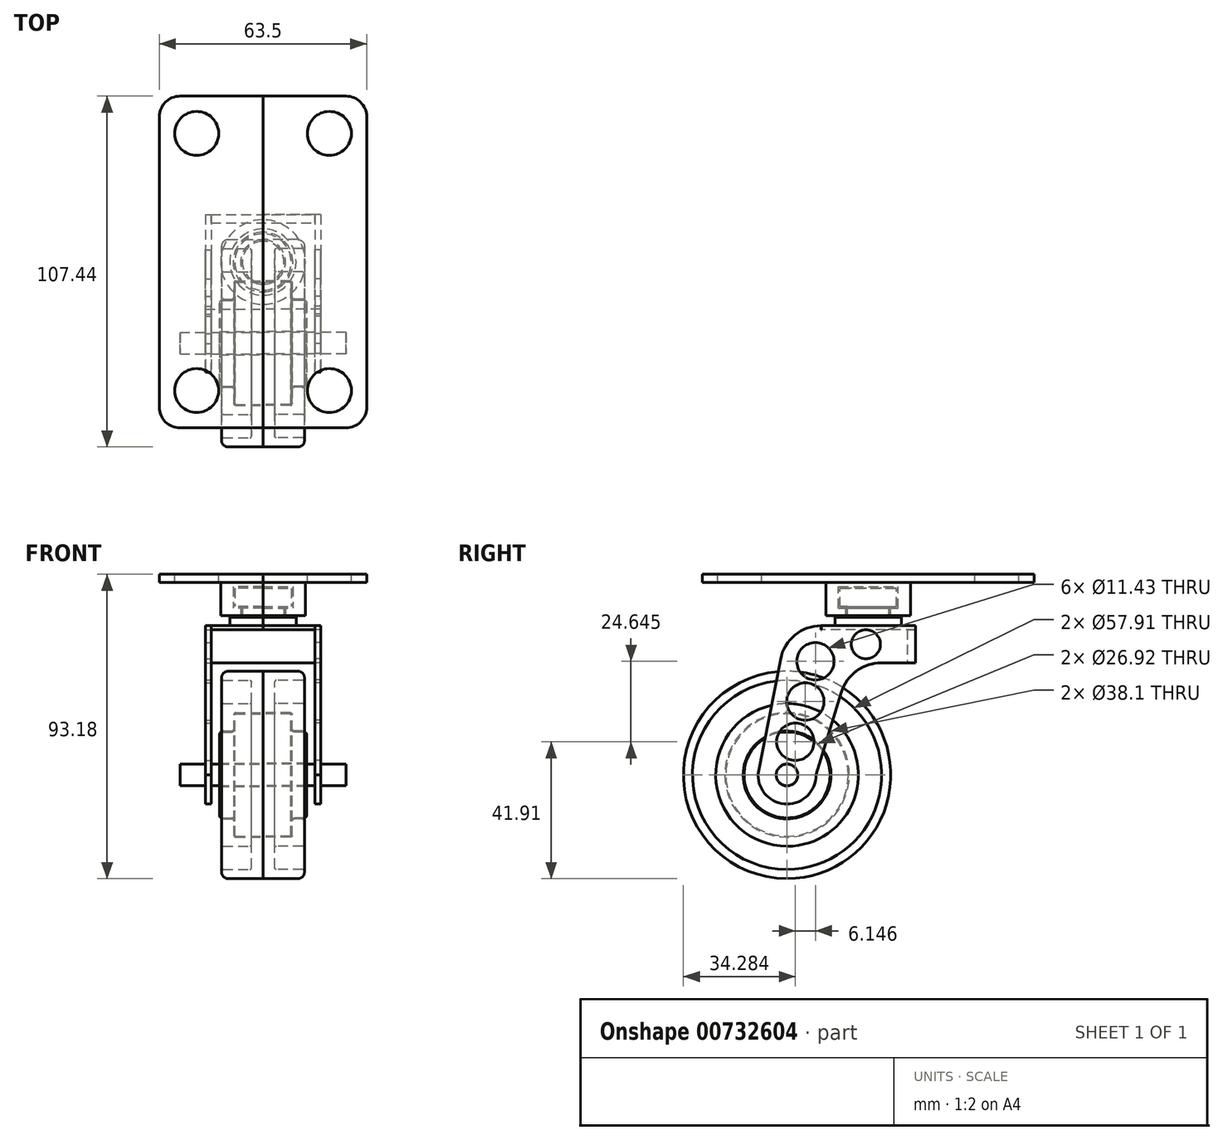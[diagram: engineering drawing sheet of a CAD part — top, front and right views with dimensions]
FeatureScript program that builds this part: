
annotation { "Feature Type Name" : "Feature", "Feature Type Description" : "" }
export const myFeature = defineFeature(function(context is Context, id is Id, definition is map)
    precondition{}
    {
        {
            var Q0;
            Q0=qCreatedBy(makeId("Front.planeOp"),FACE);
            var sketch = newSketch(context, id + "F0", { "sketchPlane" : qUnion([Q0])});
            skLineSegment(sketch, "E0.top", {"start": v(2.03, 31.75) * mm, "end": v(12.7, 31.75) * mm});
            skLineSegment(sketch, "E0.left", {"start": v(0, 29.46) * mm, "end": v(0, 29.72) * mm});
            skLineSegment(sketch, "E1", {"start": v(0, 0) * mm, "end": v(36.08, 0) * mm, "construction": true});
            skLineSegment(sketch, "E2.top", {"start": v(4.32, 19.05) * mm, "end": v(12.7, 19.05) * mm});
            skLineSegment(sketch, "E2.left", {"start": v(3.81, 14.22) * mm, "end": v(3.8, 18.54) * mm});
            skLineSegment(sketch, "E3", {"start": v(0.76, 13.46) * mm, "end": v(3.05, 13.46) * mm});
            skLineSegment(sketch, "E4", {"start": v(12.7, 31.75) * mm, "end": v(12.7, 19.05) * mm});
            skPoint(sketch, "E5.visualSharp", {"position": v(0, 31.75) * mm});
            skArc(sketch, "E5.filletArc", {"start": v(2.03, 31.75) * mm, "mid": v(0.6, 31.15) * mm, "end": v(0, 29.72) * mm});
            skArc(sketch, "E6.filletArc", {"start": v(3.05, 13.46) * mm, "mid": v(3.59, 13.69) * mm, "end": v(3.81, 14.22) * mm});
            skArc(sketch, "E7.filletArc", {"start": v(0, 14.22) * mm, "mid": v(0.22, 13.69) * mm, "end": v(0.76, 13.46) * mm});
            skPoint(sketch, "E8.visualSharp", {"position": v(3.8, 19.05) * mm});
            skArc(sketch, "E8.filletArc", {"start": v(4.32, 19.05) * mm, "mid": v(3.96, 18.9) * mm, "end": v(3.81, 18.54) * mm});
            skLineSegment(sketch, "E9.0", {"start": v(4.32, 18.75) * mm, "end": v(12.7, 18.75) * mm});
            skLineSegment(sketch, "E10.0", {"start": v(3.8, 14.22) * mm, "end": v(3.8, 18.54) * mm});
            skArc(sketch, "E11.0", {"start": v(3.05, 13.16) * mm, "mid": v(3.8, 13.47) * mm, "end": v(4.11, 14.22) * mm});
            skLineSegment(sketch, "E11.1", {"start": v(0.13, 13.16) * mm, "end": v(3.05, 13.16) * mm});
            skArc(sketch, "E11.5", {"start": v(4.32, 18.75) * mm, "mid": v(4.17, 18.69) * mm, "end": v(4.11, 18.54) * mm});
            skLineSegment(sketch, "E12", {"start": v(4.11, 18.54) * mm, "end": v(4.11, 14.22) * mm});
            skLineSegment(sketch, "E13", {"start": v(12.7, 18.75) * mm, "end": v(12.7, 3.56) * mm});
            skPoint(sketch, "E14.visualSharp", {"position": v(0, 13.16) * mm});
            skLineSegment(sketch, "E15.bottom", {"start": v(12.7, 3.56) * mm, "end": v(-0.63, 3.56) * mm});
            skPoint(sketch, "E15.middle", {"position": v(0, 0) * mm});
            skPoint(sketch, "E15.right.end.orphan", {"position": v(-12.7, -3.56) * mm});
            skPoint(sketch, "E15.right.start.orphan", {"position": v(-12.7, 3.56) * mm});
            skPoint(sketch, "E16.orphan", {"position": v(12.7, -3.56) * mm});
            skLineSegment(sketch, "E17.0", {"start": v(-0.63, 3.56) * mm, "end": v(-0.63, 12.4) * mm});
            skPoint(sketch, "E18.visualSharp", {"position": v(-0.63, 13.16) * mm});
            skArc(sketch, "E18.filletArc", {"start": v(0.13, 13.16) * mm, "mid": v(-0.41, 12.93) * mm, "end": v(-0.63, 12.4) * mm});
            skLineSegment(sketch, "E19.bottom", {"start": v(0.5, 28.96) * mm, "end": v(8.64, 28.96) * mm});
            skLineSegment(sketch, "E19.top", {"start": v(0.5, 21.84) * mm, "end": v(8.64, 21.84) * mm});
            skLineSegment(sketch, "E19.left", {"start": v(0, 21.34) * mm, "end": v(0, 14.22) * mm});
            skLineSegment(sketch, "E19.right", {"start": v(9.14, 28.45) * mm, "end": v(9.14, 22.35) * mm});
            skArc(sketch, "E20.filletArc", {"start": v(0, 29.46) * mm, "mid": v(0.15, 29.1) * mm, "end": v(0.5, 28.96) * mm});
            skPoint(sketch, "E21.visualSharp", {"position": v(9.14, 28.96) * mm});
            skArc(sketch, "E21.filletArc", {"start": v(9.14, 28.45) * mm, "mid": v(9, 28.8) * mm, "end": v(8.64, 28.96) * mm});
            skPoint(sketch, "E22.visualSharp", {"position": v(9.14, 21.84) * mm});
            skArc(sketch, "E22.filletArc", {"start": v(8.64, 21.84) * mm, "mid": v(9, 22) * mm, "end": v(9.14, 22.35) * mm});
            skArc(sketch, "E23.filletArc", {"start": v(0.5, 21.84) * mm, "mid": v(0.15, 21.7) * mm, "end": v(0, 21.34) * mm});
            skSolve(sketch);
        }
        {
            var Q0;
            Q0=makeQuery(id+"F0.imprint","IMPRINT",FACE,{"disambiguationData":[TD([[makeQuery(id+"F0.imprint","IMPRINT",EDGE,{"derivedFrom":sQuery(id+"F0.wireOp",EDGE,"E0.top")}),-1.0]])]});
            var Q1;
            Q1=makeQuery(id+"F0.imprint","IMPRINT",FACE,{"disambiguationData":[TD([[makeQuery(id+"F0.imprint","IMPRINT",EDGE,{"derivedFrom":sQuery(id+"F0.wireOp",EDGE,"E9.0")}),-1.0]])]});
            var Q2;
            Q2=sQuery(id+"F0.wireOp",EDGE,"E1");
            revolve(context, id + "F1", {"surfaceOperationType" : NewSurfaceOperationType.NEW, "entities" : qUnion([Q0, Q1]), "axis" : qUnion([Q2]), "revolveType" : RevolveType.ONE_DIRECTION, "oppositeDirection" : true, "angle" : 360 * degree});
        }
        {
            var Q0;
            Q0=makeQuery(id+"F1.opRevolve","SWEPT_FACE",FACE,{"disambiguationData":[OSD([sQuery(id+"F0.wireOp",EDGE,"E17.0")])]});
            cPlane(context, id + "F2", {"entities" : qUnion([Q0]), "cplaneType" : CPlaneType.OFFSET, "offset" : 2.54 * mm, "width" : 152.4 * mm, "height" : 152.4 * mm});
        }
        {
            var Q0;
            Q0=makeQuery(id+"F1.opRevolve","SWEPT_FACE",FACE,{"disambiguationData":[OSD([sQuery(id+"F0.wireOp",EDGE,"E13")])]});
            var sketch = newSketch(context, id + "F3", { "sketchPlane" : qUnion([Q0])});
            skCircle(sketch, "E24", {"center": v(0, 0) * mm, "radius": 3.3 * mm});
            skSolve(sketch);
        }
        {
            var Q0;
            Q0 = qSketchRegion(id + "F3", true);
            extrude(context, id + "F4", {"entities" : qUnion([Q0]), "oppositeDirection" : true, "depth" : 25.4 * mm, "offsetDistance" : 25.4 * mm});
        }
        {
            var Q0;
            Q0=qCreatedBy(id+"F2.planeOp",FACE);
            var sketch = newSketch(context, id + "F5", { "sketchPlane" : qUnion([Q0])});
            skCircle(sketch, "E25", {"center": v(0, 0) * mm, "radius": 3.3 * mm});
            skArc(sketch, "E26", {"start": v(-8.9, 0) * mm, "mid": v(0, -8.9) * mm, "end": v(8.9, 0) * mm});
            skLineSegment(sketch, "E27.bottom", {"start": v(-39.37, 45.72) * mm, "end": v(-10.47, 45.72) * mm});
            skLineSegment(sketch, "E27.top", {"start": v(-39.37, 34.3) * mm, "end": v(-28.77, 34.3) * mm});
            skLineSegment(sketch, "E27.left", {"start": v(-39.37, 45.72) * mm, "end": v(-39.37, 34.3) * mm});
            skLineSegment(sketch, "E28", {"start": v(8.9, 0) * mm, "end": v(2, 35.44) * mm});
            skLineSegment(sketch, "E29", {"start": v(-8.89, 0) * mm, "end": v(-16.63, 25.3) * mm});
            skPoint(sketch, "E30.visualSharp", {"position": v(-19.38, 34.3) * mm});
            skArc(sketch, "E30.filletArc", {"start": v(-16.63, 25.3) * mm, "mid": v(-21.22, 31.8) * mm, "end": v(-28.77, 34.3) * mm});
            skPoint(sketch, "E31.visualSharp", {"position": v(0, 45.72) * mm});
            skArc(sketch, "E31.filletArc", {"start": v(2, 35.44) * mm, "mid": v(-2.4, 42.82) * mm, "end": v(-10.47, 45.72) * mm});
            skCircle(sketch, "E32", {"center": v(-2.53, 10.16) * mm, "radius": 5.72 * mm});
            skCircle(sketch, "E33", {"center": v(-5.6, 22.48) * mm, "radius": 5.72 * mm});
            skCircle(sketch, "E34", {"center": v(-8.68, 34.8) * mm, "radius": 5.72 * mm});
            skCircle(sketch, "E35", {"center": v(-24.13, 40) * mm, "radius": 4.45 * mm});
            skLineSegment(sketch, "E36", {"start": v(-39.37, 40) * mm, "end": v(-24.13, 40) * mm, "construction": true});
            skLineSegment(sketch, "E37", {"start": v(0, 0) * mm, "end": v(-8.68, 34.8) * mm, "construction": true});
            skLineSegment(sketch, "E38", {"start": v(-5.6, 22.48) * mm, "end": v(-5.6, 22.48) * mm});
            skSolve(sketch);
        }
        {
            var Q0;
            Q0 = qSketchRegion(id + "F5", true);
            extrude(context, id + "F6", {"entities" : qUnion([Q0]), "operationType" : NewBodyOperationType.ADD, "depth" : 1.78 * mm, "offsetDistance" : 25.4 * mm});
        }
        {
            var Q0;
            Q0=makeQuery(id+"F6.opExtrude","SWEPT_FACE",FACE,{"disambiguationData":[OSD([sQuery(id+"F5.wireOp",EDGE,"E27.bottom")])]});
            var sketch = newSketch(context, id + "F7", { "sketchPlane" : qUnion([Q0])});
            skLineSegment(sketch, "E39.bottom", {"start": v(-4.95, 39.37) * mm, "end": v(12.7, 39.37) * mm});
            skLineSegment(sketch, "E39.top", {"start": v(-4.95, 10.41) * mm, "end": v(12.7, 10.41) * mm});
            skLineSegment(sketch, "E39.left", {"start": v(-4.95, 39.37) * mm, "end": v(-4.95, 10.41) * mm});
            skLineSegment(sketch, "E39.right", {"start": v(12.7, 39.37) * mm, "end": v(12.7, 10.41) * mm});
            skArc(sketch, "E40", {"start": v(12.7, 35.81) * mm, "mid": v(1.78, 24.9) * mm, "end": v(12.7, 13.97) * mm});
            skSolve(sketch);
        }
        {
            var Q0;
            {var subQ3=sQuery(id+"F7.wireOp",EDGE,"E39.top");Q0=makeQuery(id+"F7.imprint","IMPRINT",FACE,{"disambiguationData":[TD([[makeQuery(id+"F7.imprint","IMPRINT",EDGE,{"derivedFrom":subQ3}),1.0]])]});}
            var Q1;
            {var subQ0=sQuery(id+"F7.wireOp",EDGE,"E40");Q1=makeQuery(id+"F7.imprint","IMPRINT",FACE,{"disambiguationData":[TD([[makeQuery(id+"F7.imprint","IMPRINT",EDGE,{"derivedFrom":subQ0}),1.0]])]});}
            extrude(context, id + "F8", {"entities" : qUnion([Q0, Q1]), "oppositeDirection" : true, "depth" : 1.27 * mm, "offsetDistance" : 25.4 * mm});
        }
        {
            var Q0;
            Q0=makeQuery(id+"F8.opExtrude","SWEPT_FACE",FACE,{"disambiguationData":[OSD([sQuery(id+"F7.wireOp",EDGE,"E39.right")])]});
            var sketch = newSketch(context, id + "F9", { "sketchPlane" : qUnion([Q0])});
            skLineSegment(sketch, "E41.bottom", {"start": v(24.9, 44.45) * mm, "end": v(35.05, 44.45) * mm});
            skLineSegment(sketch, "E41.top", {"start": v(31.24, 48.26) * mm, "end": v(35.05, 48.26) * mm});
            skLineSegment(sketch, "E41.right", {"start": v(35.05, 44.45) * mm, "end": v(35.05, 48.26) * mm});
            skLineSegment(sketch, "E42.right", {"start": v(31.24, 48.26) * mm, "end": v(31.24, 51.52) * mm});
            skLineSegment(sketch, "E43.bottom", {"start": v(31.24, 51.52) * mm, "end": v(33.53, 51.52) * mm});
            skLineSegment(sketch, "E43.top", {"start": v(24.9, 57.1) * mm, "end": v(33.53, 57.1) * mm});
            skLineSegment(sketch, "E43.right", {"start": v(33.53, 51.52) * mm, "end": v(33.53, 57.1) * mm});
            skLineSegment(sketch, "E44.trimOffspring", {"start": v(24.9, 57.1) * mm, "end": v(24.9, 57.15) * mm, "construction": true});
            skLineSegment(sketch, "E45", {"start": v(24.9, 61.43) * mm, "end": v(24.9, 44.45) * mm, "construction": true});
            skLineSegment(sketch, "E46", {"start": v(37.85, 48.77) * mm, "end": v(31.75, 48.77) * mm});
            skLineSegment(sketch, "E47", {"start": v(31.75, 48.77) * mm, "end": v(31.75, 51.01) * mm});
            skLineSegment(sketch, "E48", {"start": v(31.75, 51.01) * mm, "end": v(34.04, 51.01) * mm});
            skLineSegment(sketch, "E49", {"start": v(34.04, 51.01) * mm, "end": v(34.04, 57.62) * mm});
            skLineSegment(sketch, "E50", {"start": v(34.04, 57.62) * mm, "end": v(24.9, 57.62) * mm});
            skLineSegment(sketch, "E51", {"start": v(24.9, 61.43) * mm, "end": v(37.85, 61.43) * mm});
            skLineSegment(sketch, "E52", {"start": v(37.85, 61.43) * mm, "end": v(37.85, 48.77) * mm});
            skLineSegment(sketch, "E53", {"start": v(24.9, 61.43) * mm, "end": v(24.9, 57.62) * mm});
            skLineSegment(sketch, "E54", {"start": v(24.9, 57.15) * mm, "end": v(24.9, 44.45) * mm});
            skSolve(sketch);
        }
        {
            var Q0;
            Q0 = qSketchRegion(id + "F9", true);
            var Q1;
            Q1=sQuery(id+"F9.wireOp",EDGE,"E45");
            revolve(context, id + "F10", {"operationType" : NewBodyOperationType.ADD, "surfaceOperationType" : NewSurfaceOperationType.NEW, "entities" : qUnion([Q0]), "axis" : qUnion([Q1]), "revolveType" : RevolveType.ONE_DIRECTION, "oppositeDirection" : true, "angle" : 180 * degree});
        }
        {
            var Q0;
            Q0=makeQuery(id+"F10.opRevolve","SWEPT_FACE",FACE,{"disambiguationData":[OSD([sQuery(id+"F9.wireOp",EDGE,"E51")])]});
            var sketch = newSketch(context, id + "F11", { "sketchPlane" : qUnion([Q0])});
            skPoint(sketch, "E55.orphan", {"position": v(12.7, 24.9) * mm});
            skLineSegment(sketch, "E56.top", {"start": v(12.7, 75.7) * mm, "end": v(-12.7, 75.7) * mm});
            skLineSegment(sketch, "E56.left", {"start": v(12.7, -25.9) * mm, "end": v(12.7, 75.7) * mm});
            skLineSegment(sketch, "E56.right", {"start": v(-19.05, -19.56) * mm, "end": v(-19.05, 69.34) * mm});
            skLineSegment(sketch, "E57", {"start": v(-12.7, -25.9) * mm, "end": v(12.7, -25.9) * mm});
            skCircle(sketch, "E58", {"center": v(-7.62, 64.26) * mm, "radius": 6.73 * mm});
            skCircle(sketch, "E59", {"center": v(-7.62, -14.48) * mm, "radius": 6.73 * mm});
            skPoint(sketch, "E60.visualSharp", {"position": v(-19.05, 75.7) * mm});
            skArc(sketch, "E60.filletArc", {"start": v(-12.7, 75.7) * mm, "mid": v(-17.2, 73.83) * mm, "end": v(-19.05, 69.34) * mm});
            skPoint(sketch, "E61.visualSharp", {"position": v(-19.05, -25.9) * mm});
            skArc(sketch, "E61.filletArc", {"start": v(-19.05, -19.56) * mm, "mid": v(-17.2, -24.05) * mm, "end": v(-12.7, -25.9) * mm});
            skSolve(sketch);
        }
        {
            var Q0;
            Q0 = qSketchRegion(id + "F11", true);
            extrude(context, id + "F12", {"entities" : qUnion([Q0]), "operationType" : NewBodyOperationType.ADD, "oppositeDirection" : true, "depth" : 2.54 * mm, "offsetDistance" : 25.4 * mm});
        }
        {
            var Q0;
            Q0=makeQuery(id+"F10.opRevolve","SWEPT_BODY",BODY,{"disambiguationData":[OSD([sQuery(id+"F9.wireOp",EDGE,"E46"),sQuery(id+"F9.wireOp",EDGE,"E47"),sQuery(id+"F9.wireOp",EDGE,"E48"),sQuery(id+"F9.wireOp",EDGE,"E49"),sQuery(id+"F9.wireOp",EDGE,"E50"),sQuery(id+"F9.wireOp",EDGE,"E51"),sQuery(id+"F9.wireOp",EDGE,"E52"),sQuery(id+"F9.wireOp",EDGE,"E53")])]});
            var Q1;
            Q1=makeQuery(id+"F8.opExtrude","SWEPT_BODY",BODY,{"disambiguationData":[OSD([sQuery(id+"F5.wireOp",EDGE,"E27.bottom"),sQuery(id+"F5.wireOp",EDGE,"E31.filletArc"),sQuery(id+"F7.wireOp",EDGE,"E39.bottom"),sQuery(id+"F7.wireOp",EDGE,"E39.top"),sQuery(id+"F7.wireOp",EDGE,"E39.left"),sQuery(id+"F7.wireOp",EDGE,"E39.right")])]});
            var Q2;
            Q2=makeQuery(id+"F1.opRevolve","SWEPT_BODY",BODY,{"disambiguationData":[OSD([sQuery(id+"F0.wireOp",EDGE,"E0.top"),sQuery(id+"F0.wireOp",EDGE,"E0.left"),sQuery(id+"F0.wireOp",EDGE,"E2.top"),sQuery(id+"F0.wireOp",EDGE,"E3"),sQuery(id+"F0.wireOp",EDGE,"E4"),sQuery(id+"F0.wireOp",EDGE,"E5.filletArc"),sQuery(id+"F0.wireOp",EDGE,"E6.filletArc"),sQuery(id+"F0.wireOp",EDGE,"E7.filletArc"),sQuery(id+"F0.wireOp",EDGE,"E8.filletArc"),sQuery(id+"F0.wireOp",EDGE,"E10.0"),sQuery(id+"F0.wireOp",EDGE,"E19.bottom"),sQuery(id+"F0.wireOp",EDGE,"E19.top"),sQuery(id+"F0.wireOp",EDGE,"E19.left"),sQuery(id+"F0.wireOp",EDGE,"E19.right"),sQuery(id+"F0.wireOp",EDGE,"E20.filletArc"),sQuery(id+"F0.wireOp",EDGE,"E21.filletArc"),sQuery(id+"F0.wireOp",EDGE,"E22.filletArc"),sQuery(id+"F0.wireOp",EDGE,"E23.filletArc")])]});
            var Q3;
            Q3=makeQuery(id+"F1.opRevolve","SWEPT_BODY",BODY,{"disambiguationData":[OSD([sQuery(id+"F0.wireOp",EDGE,"E9.0"),sQuery(id+"F0.wireOp",EDGE,"E11.0"),sQuery(id+"F0.wireOp",EDGE,"E11.1"),sQuery(id+"F0.wireOp",EDGE,"E11.5"),sQuery(id+"F0.wireOp",EDGE,"E12"),sQuery(id+"F0.wireOp",EDGE,"E13"),sQuery(id+"F0.wireOp",EDGE,"E15.bottom"),sQuery(id+"F0.wireOp",EDGE,"E17.0"),sQuery(id+"F0.wireOp",EDGE,"E18.filletArc")])]});
            var Q4;
            Q4=makeQuery(id+"F4.opExtrude","SWEPT_BODY",BODY,{"disambiguationData":[OSD([sQuery(id+"F3.wireOp",EDGE,"E24")])]});
            var Q5;
            Q5=makeQuery(id+"F1.opRevolve","SWEPT_FACE",FACE,{"disambiguationData":[OSD([sQuery(id+"F0.wireOp",EDGE,"E4")])]});
            mirror(context, id + "F13", {"entities" : qUnion([Q0, Q1, Q2, Q3, Q4]), "mirrorPlane" : qUnion([Q5])});
        }
        {
            var Q0;
            Q0=makeQuery(id+"F6.opExtrude","SWEPT_FACE",FACE,{"disambiguationData":[OSD([sQuery(id+"F5.wireOp",EDGE,"E27.left")])]});
            var sketch = newSketch(context, id + "F14", { "sketchPlane" : qUnion([Q0])});
            skLineSegment(sketch, "E62.bottom", {"start": v(3.17, 44.45) * mm, "end": v(-28.57, 44.45) * mm});
            skLineSegment(sketch, "E62.top", {"start": v(3.18, 34.3) * mm, "end": v(-28.57, 34.3) * mm});
            skLineSegment(sketch, "E62.left", {"start": v(3.17, 44.45) * mm, "end": v(3.17, 34.3) * mm});
            skLineSegment(sketch, "E62.right", {"start": v(-28.57, 44.45) * mm, "end": v(-28.57, 34.3) * mm});
            skSolve(sketch);
        }
        {
            var Q0;
            Q0 = qSketchRegion(id + "F14", true);
            extrude(context, id + "F15", {"entities" : qUnion([Q0]), "oppositeDirection" : true, "depth" : 2.54 * mm, "offsetDistance" : 25.4 * mm});
        }
    });
